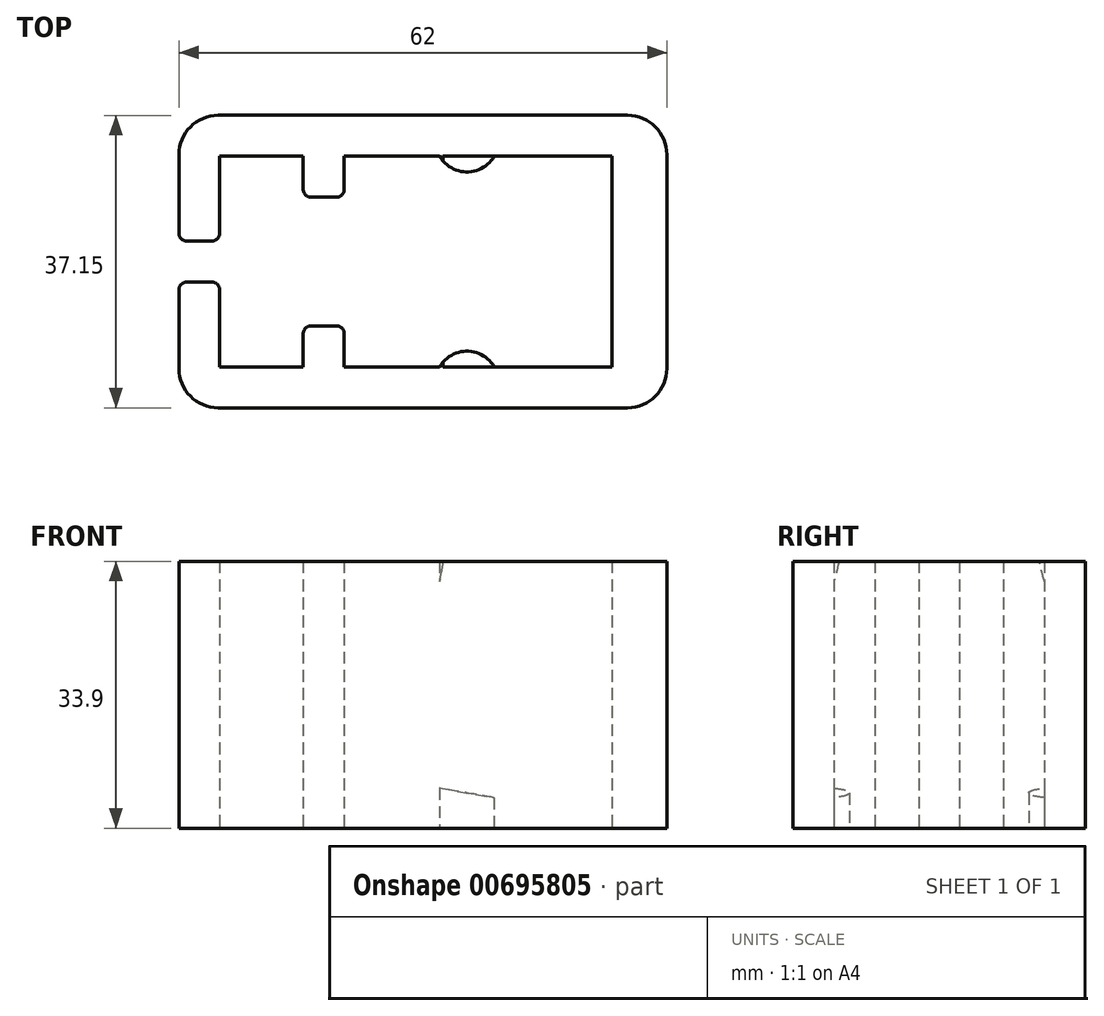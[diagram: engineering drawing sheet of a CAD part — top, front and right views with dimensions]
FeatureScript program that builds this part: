
annotation { "Feature Type Name" : "Feature", "Feature Type Description" : "" }
export const myFeature = defineFeature(function(context is Context, id is Id, definition is map)
    precondition{}
    {
        {
            var Q0;
            Q0=qCreatedBy(makeId("Top.planeOp"),FACE);
            var sketch = newSketch(context, id + "F0", { "sketchPlane" : qUnion([Q0])});
            skLineSegment(sketch, "E0.bottom", {"start": v(-11.22, 5.32) * mm, "end": v(22.78, 5.32) * mm, "construction": true});
            skLineSegment(sketch, "E0.top", {"start": v(-11.22, -17.43) * mm, "end": v(22.78, -17.43) * mm, "construction": true});
            skLineSegment(sketch, "E0.left", {"start": v(-11.22, 5.32) * mm, "end": v(-11.22, -17.43) * mm, "construction": true});
            skLineSegment(sketch, "E0.right", {"start": v(22.78, 5.32) * mm, "end": v(22.78, -17.43) * mm, "construction": true});
            skLineSegment(sketch, "E1", {"start": v(22.78, 7.32) * mm, "end": v(7.84, 7.32) * mm});
            skLineSegment(sketch, "E2", {"start": v(-11.22, 7.32) * mm, "end": v(-11.22, -19.43) * mm});
            skLineSegment(sketch, "E3", {"start": v(-11.22, -19.43) * mm, "end": v(0.91, -19.43) * mm});
            skLineSegment(sketch, "E4", {"start": v(22.78, -19.43) * mm, "end": v(22.78, 7.32) * mm});
            skArc(sketch, "E5", {"start": v(0.91, 7.32) * mm, "mid": v(4.38, 5.32) * mm, "end": v(7.84, 7.32) * mm});
            skArc(sketch, "E6", {"start": v(7.84, -19.43) * mm, "mid": v(4.38, -17.43) * mm, "end": v(0.91, -19.43) * mm});
            skLineSegment(sketch, "E7.bottom", {"start": v(-27.22, 12.52) * mm, "end": v(24.78, 12.52) * mm});
            skLineSegment(sketch, "E7.top", {"start": v(-27.22, -24.63) * mm, "end": v(24.78, -24.63) * mm});
            skLineSegment(sketch, "E7.left", {"start": v(-32.22, 7.52) * mm, "end": v(-32.22, -3.45) * mm});
            skLineSegment(sketch, "E7.right", {"start": v(29.78, 7.52) * mm, "end": v(29.78, -19.63) * mm});
            skLineSegment(sketch, "E8.top", {"start": v(-11.22, 2.12) * mm, "end": v(-16.42, 2.12) * mm});
            skLineSegment(sketch, "E8.left", {"start": v(-11.22, 7.32) * mm, "end": v(-11.22, 2.12) * mm});
            skLineSegment(sketch, "E8.right", {"start": v(-16.42, 7.32) * mm, "end": v(-16.42, 2.12) * mm});
            skLineSegment(sketch, "E9.top", {"start": v(-11.22, -14.23) * mm, "end": v(-16.42, -14.23) * mm});
            skLineSegment(sketch, "E9.left", {"start": v(-11.22, -19.43) * mm, "end": v(-11.22, -14.23) * mm});
            skLineSegment(sketch, "E9.right", {"start": v(-16.42, -19.43) * mm, "end": v(-16.42, -14.23) * mm});
            skLineSegment(sketch, "E10", {"start": v(-16.42, 7.32) * mm, "end": v(-27.02, 7.32) * mm});
            skLineSegment(sketch, "E11", {"start": v(-27.02, 7.32) * mm, "end": v(-27.02, -3.45) * mm});
            skLineSegment(sketch, "E12", {"start": v(-27.02, -19.43) * mm, "end": v(-16.42, -19.43) * mm});
            skPoint(sketch, "E13.visualSharp", {"position": v(-32.22, 12.52) * mm});
            skArc(sketch, "E13.filletArc", {"start": v(-27.22, 12.52) * mm, "mid": v(-30.76, 11.06) * mm, "end": v(-32.22, 7.52) * mm});
            skPoint(sketch, "E14.visualSharp", {"position": v(29.78, 12.52) * mm});
            skArc(sketch, "E14.filletArc", {"start": v(29.78, 7.52) * mm, "mid": v(28.31, 11.06) * mm, "end": v(24.78, 12.52) * mm});
            skPoint(sketch, "E15.visualSharp", {"position": v(29.78, -24.63) * mm});
            skArc(sketch, "E15.filletArc", {"start": v(24.78, -24.63) * mm, "mid": v(28.31, -23.16) * mm, "end": v(29.78, -19.63) * mm});
            skPoint(sketch, "E16.visualSharp", {"position": v(-32.22, -24.63) * mm});
            skArc(sketch, "E16.filletArc", {"start": v(-32.22, -19.63) * mm, "mid": v(-30.76, -23.16) * mm, "end": v(-27.22, -24.63) * mm});
            skLineSegment(sketch, "E17", {"start": v(-32.22, -3.45) * mm, "end": v(-27.02, -3.45) * mm});
            skLineSegment(sketch, "E18", {"start": v(-32.22, -8.65) * mm, "end": v(-27.02, -8.65) * mm});
            skLineSegment(sketch, "E19.trimOffspring", {"start": v(-27.02, -8.65) * mm, "end": v(-27.02, -19.43) * mm});
            skLineSegment(sketch, "E20.trimOffspring", {"start": v(-32.22, -8.65) * mm, "end": v(-32.22, -19.63) * mm});
            skLineSegment(sketch, "E21.trimOffspring", {"start": v(0.91, 7.32) * mm, "end": v(-11.22, 7.32) * mm});
            skLineSegment(sketch, "E22.trimOffspring", {"start": v(7.84, -19.43) * mm, "end": v(22.78, -19.43) * mm});
            skSolve(sketch);
        }
        {
            var Q0;
            Q0=makeQuery(id+"F0.imprint","IMPRINT",FACE,{"disambiguationData":[TD([[makeQuery(id+"F0.imprint","IMPRINT",EDGE,{"derivedFrom":sQuery(id+"F0.wireOp",EDGE,"E1")}),-1.0]])]});
            extrude(context, id + "F1", {"entities" : qUnion([Q0]), "depth" : 33.9 * mm, "offsetDistance" : 25 * mm});
        }
        {
            var Q0;
            Q0=makeQuery(id+"F1.opExtrude","SWEPT_EDGE",EDGE,{"disambiguationData":[OSD([sQuery(id+"F0.wireOp",EDGE,"E9.top"),sQuery(id+"F0.wireOp",EDGE,"E9.right")])]});
            var Q1;
            Q1=makeQuery(id+"F1.opExtrude","SWEPT_EDGE",EDGE,{"disambiguationData":[OSD([sQuery(id+"F0.wireOp",EDGE,"E2"),sQuery(id+"F0.wireOp",EDGE,"E9.top"),sQuery(id+"F0.wireOp",EDGE,"E9.left")])]});
            var Q2;
            Q2=makeQuery(id+"F1.opExtrude","SWEPT_EDGE",EDGE,{"disambiguationData":[OSD([sQuery(id+"F0.wireOp",EDGE,"E2"),sQuery(id+"F0.wireOp",EDGE,"E8.top"),sQuery(id+"F0.wireOp",EDGE,"E8.left")])]});
            var Q3;
            Q3=makeQuery(id+"F1.opExtrude","SWEPT_EDGE",EDGE,{"disambiguationData":[OSD([sQuery(id+"F0.wireOp",EDGE,"E8.top"),sQuery(id+"F0.wireOp",EDGE,"E8.right")])]});
            var Q4;
            Q4=makeQuery(id+"F1.opExtrude","SWEPT_EDGE",EDGE,{"disambiguationData":[OSD([sQuery(id+"F0.wireOp",EDGE,"E18"),sQuery(id+"F0.wireOp",EDGE,"E19.trimOffspring")])]});
            var Q5;
            Q5=makeQuery(id+"F1.opExtrude","SWEPT_EDGE",EDGE,{"disambiguationData":[OSD([sQuery(id+"F0.wireOp",EDGE,"E18"),sQuery(id+"F0.wireOp",EDGE,"E20.trimOffspring")])]});
            var Q6;
            Q6=makeQuery(id+"F1.opExtrude","SWEPT_EDGE",EDGE,{"disambiguationData":[OSD([sQuery(id+"F0.wireOp",EDGE,"E11"),sQuery(id+"F0.wireOp",EDGE,"E17")])]});
            var Q7;
            Q7=makeQuery(id+"F1.opExtrude","SWEPT_EDGE",EDGE,{"disambiguationData":[OSD([sQuery(id+"F0.wireOp",EDGE,"E7.left"),sQuery(id+"F0.wireOp",EDGE,"E17")])]});
            fillet(context, id + "F2", {"entities" : qUnion([Q0, Q1, Q2, Q3, Q4, Q5, Q6, Q7]), "radius" : 1 * mm, "tangentPropagation" : true, "allowEdgeOverflow" : false});
        }
        {
            var Q0;
            Q0=makeQuery(id+"F1.opExtrude","CAP_EDGE",EDGE,{"disambiguationData":[OSD([sQuery(id+"F0.wireOp",EDGE,"E7.right")])],"isStart":true});
            cPlane(context, id + "F3", {"entities" : qUnion([Q0]), "cplaneType" : CPlaneType.LINE_ANGLE, "offset" : 3 * mm, "angle" : 10 * degree, "oppositeDirection" : true, "width" : 150 * mm, "height" : 150 * mm});
        }
        {
            var Q0;
            Q0=qCreatedBy(id+"F3.planeOp",FACE);
            var sketch = newSketch(context, id + "F4", { "sketchPlane" : qUnion([Q0])});
            skLineSegment(sketch, "E23.bottom", {"start": v(-4.54, 19.43) * mm, "end": v(11.1, 19.43) * mm});
            skLineSegment(sketch, "E23.top", {"start": v(-4.54, -7.32) * mm, "end": v(11.1, -7.32) * mm});
            skLineSegment(sketch, "E23.left", {"start": v(-4.54, 19.43) * mm, "end": v(-4.54, -7.32) * mm});
            skLineSegment(sketch, "E23.right", {"start": v(11.1, 19.43) * mm, "end": v(11.1, -7.32) * mm});
            skSolve(sketch);
        }
        {
            var Q0;
            Q0 = qSketchRegion(id + "F4", true);
            extrude(context, id + "F5", {"entities" : qUnion([Q0]), "operationType" : NewBodyOperationType.REMOVE, "oppositeDirection" : true, "depth" : 33.1 * mm, "offsetDistance" : 25 * mm});
        }
    });
